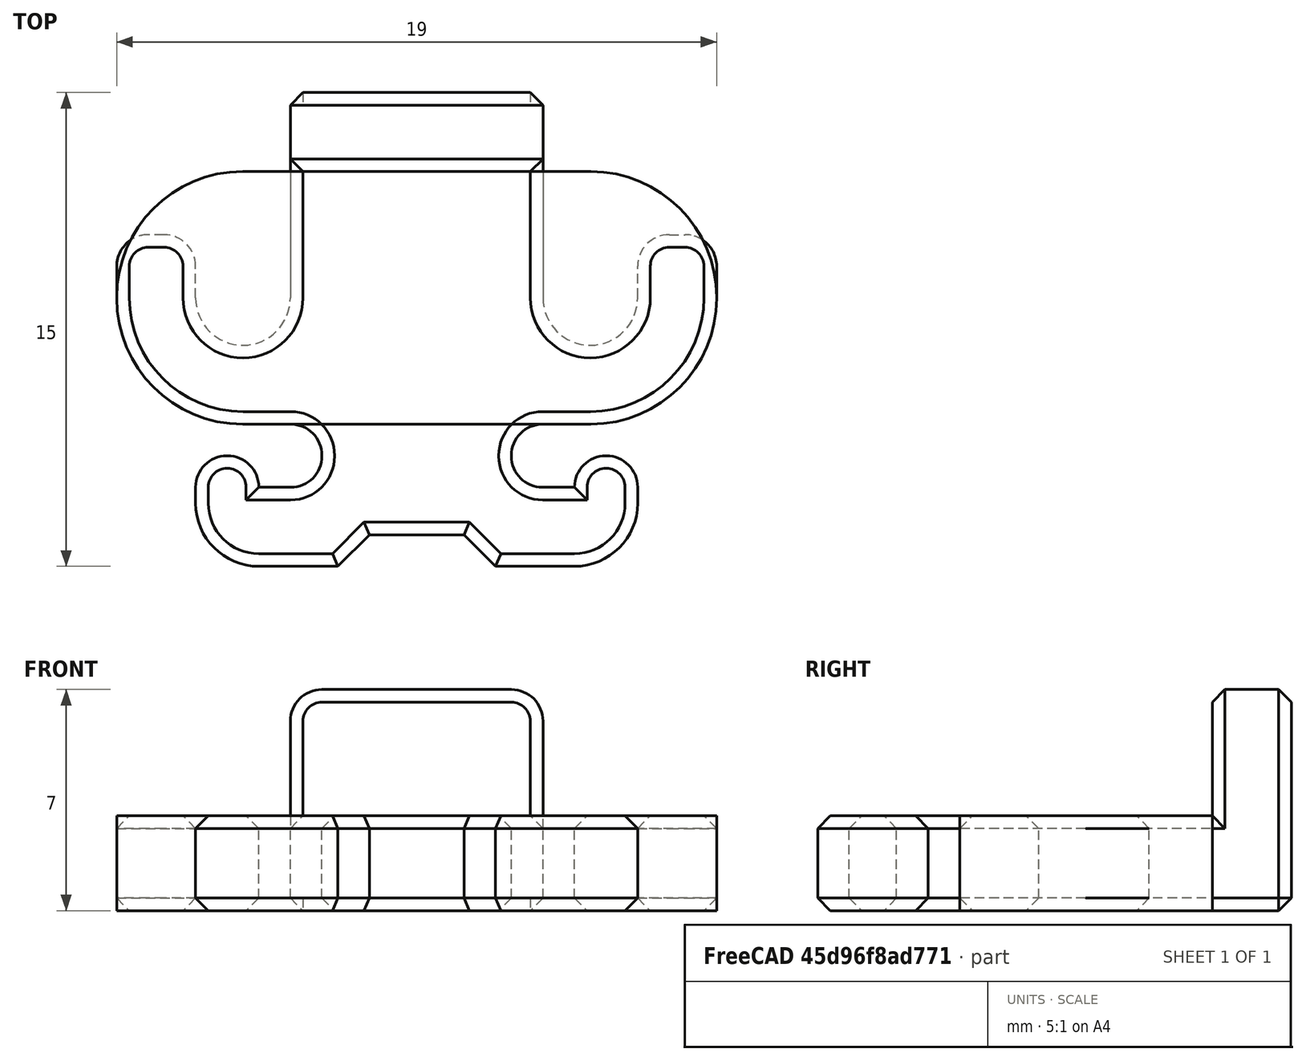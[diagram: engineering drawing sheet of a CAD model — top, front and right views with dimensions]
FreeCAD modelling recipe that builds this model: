
FCSTD DOCUMENT  (FreeCAD 0.19R24291 (Git))
Label: hb3-wire-mounter
License: Other
LicenseURL: GPL3
objects: Part::Box×13, Part::MultiFuse×7, Part::Fillet×6, Part::Cut×4, Part::Cylinder×2, Part::Chamfer×2
note: 34 computed .brp shape members not serialized (recipe doc carries the construction recipe); baked Part::Feature solids carry a one-line shape summary decoded from their .brp

FEATURE [Part::Box] Box  label="Cube"
  AttacherType = Attacher::AttachEngine3D
  Height = 3
  Length = 19
  Placement = pos=(-9.5,-4,0) rot=(0,0,1;0rad)
  Width = 8
FEATURE [Part::Cylinder] Cylinder
  Angle = 360
  AttacherType = Attacher::AttachEngine3D
  Height = 10
  Placement = pos=(5.5,0,0) rot=(0,0,1;0rad)
  Radius = 1.5
FEATURE [Part::Cylinder] Cylinder001
  Angle = 360
  AttacherType = Attacher::AttachEngine3D
  Height = 10
  Placement = pos=(-5.5,0,0) rot=(0,0,1;0rad)
  Radius = 1.5
FEATURE [Part::Box] Box001  label="Cube001"
  AttacherType = Attacher::AttachEngine3D
  Height = 10
  Length = 3
  Placement = pos=(4,0,0) rot=(0,0,1;0rad)
  Width = 10
FEATURE [Part::Box] Box002  label="Cube002"
  AttacherType = Attacher::AttachEngine3D
  Height = 10
  Length = 3
  Placement = pos=(-7,0,0) rot=(0,0,1;0rad)
  Width = 10
FEATURE [Part::Box] Box003  label="Cube003"
  AttacherType = Attacher::AttachEngine3D
  Height = 3
  Length = 19
  Placement = pos=(-9.5,-4,0) rot=(0,0,1;0rad)
  Width = 8
FEATURE [Part::Fillet] Fillet
  Base = -> Box003
  Edges = 4 edges r=3.99: [Edge1,Edge3,Edge5,Edge7]
FEATURE [Part::Box] Box004  label="Cube004"
  AttacherType = Attacher::AttachEngine3D
  Height = 7
  Length = 8
  Placement = pos=(-4,4,0) rot=(0,0,1;0rad)
  Width = 2.5
FEATURE [Part::Box] Box005  label="Cube005"
  AttacherType = Attacher::AttachEngine3D
  Height = 3
  Length = 14
  Placement = pos=(-7,-8.5,0) rot=(0,0,1;0rad)
  Width = 4.5
FEATURE [Part::Box] Box006  label="Cube006"
  AttacherType = Attacher::AttachEngine3D
  Height = 3
  Length = 2
  Placement = pos=(1.5,-6,0) rot=(0,0,1;0rad)
  Width = 2
FEATURE [Part::Box] Box007  label="Cube007"
  AttacherType = Attacher::AttachEngine3D
  Height = 3
  Length = 4
  Placement = pos=(2,-5,0) rot=(0,0,1;0rad)
  Width = 1
FEATURE [Part::Box] Box008  label="Cube008"
  AttacherType = Attacher::AttachEngine3D
  Height = 3
  Length = 2
  Placement = pos=(-3.5,-6,0) rot=(0,0,1;0rad)
  Width = 2
FEATURE [Part::Box] Box009  label="Cube009"
  AttacherType = Attacher::AttachEngine3D
  Height = 3
  Length = 4
  Placement = pos=(-6,-5,0) rot=(0,0,1;0rad)
  Width = 1
FEATURE [Part::MultiFuse] Fusion
  Shapes = -> [Box002,Cylinder,Cylinder001,Box001]
FEATURE [Part::Fillet] Fillet006
  Base = -> Box004
  Edges = 2 edges r=1: [Edge2,Edge6]
FEATURE [Part::Fillet] Fillet007
  Base = -> Box
  Edges = 2 edges r=4: [Edge1,Edge5]
FEATURE [Part::Cut] Cut
  Base = -> Fillet007
  Tool = -> Fusion
FEATURE [Part::Box] Box010  label="Cube010"
  AttacherType = Attacher::AttachEngine3D
  Height = 10
  Length = 10
  Placement = pos=(6,2,0) rot=(0,0,1;0rad)
  Width = 10
FEATURE [Part::Box] Box011  label="Cube011"
  AttacherType = Attacher::AttachEngine3D
  Height = 10
  Length = 10
  Placement = pos=(-16,2,0) rot=(0,0,1;0rad)
  Width = 10
FEATURE [Part::MultiFuse] Fusion002
  Shapes = -> [Box011,Box010]
FEATURE [Part::Cut] Cut002
  Base = -> Cut
  Tool = -> Fusion002
FEATURE [Part::Fillet] Fillet008
  Base = -> Cut002
  Edges = 4 edges r=1: [Edge2,Edge19,Edge39,Edge40]
FEATURE [Part::MultiFuse] Fusion003
  Placement = pos=(1.5,0,0) rot=(0,0,1;0rad)
  Shapes = -> [Box006,Box007]
FEATURE [Part::MultiFuse] Fusion004
  Placement = pos=(-1.5,0,0) rot=(0,0,1;0rad)
  Shapes = -> [Box009,Box008]
FEATURE [Part::MultiFuse] Fusion005
  Shapes = -> [Fusion004,Fusion003]
FEATURE [Part::Cut] Cut003
  Base = -> Box005
  Tool = -> Fusion005
FEATURE [Part::Box] Box012  label="Cube012"
  AttacherType = Attacher::AttachEngine3D
  Height = 10
  Length = 5
  Placement = pos=(-2.5,-11.5,0) rot=(0,0,1;0rad)
  Width = 4
FEATURE [Part::Chamfer] Chamfer
  Base = -> Box012
  Edges = 2 edges r=1: [Edge3,Edge7]
FEATURE [Part::Cut] Cut004
  Base = -> Cut003
  Tool = -> Chamfer
FEATURE [Part::Fillet] Fillet009
  Base = -> Cut004
  Edges = 2 edges r=2: [Edge4,Edge45]
FEATURE [Part::MultiFuse] Fusion006
  Shapes = -> [Fillet008,Fillet009]
FEATURE [Part::Fillet] Fillet010
  Base = -> Fusion006
  Edges = 8 edges r=0.99: [Edge45,Edge64,Edge95,Edge97,Edge105,Edge106,Edge108,Edge110]
FEATURE [Part::MultiFuse] Fusion007
  Refine = true
  Shapes = -> [Fillet010,Fillet006]
FEATURE [Part::Chamfer] Chamfer001
  Base = -> Fusion007
  Edges = 97 edges r=0.4: [Edge1,Edge3,Edge5,Edge6,Edge8,Edge10,Edge12,Edge13,Edge15,Edge16,Edge18,Edge20,Edge21,Edge22,Edge24,Edge25,Edge26,Edge28,Edge29,Edge31,Edge32,Edge34,Edge35,Edge37,Edge38,Edge39,Edge41,Edge43,Edge44,Edge46,Edge47,Edge48,Edge50,Edge52,Edge53,Edge55,Edge56,Edge57,Edge59,Edge61,Edge62,Edge64,Edge65,+54 more]
